# Revit family: Legrand_ElectricFireStopping_EZPathFirestopModule_Series33_Wall
name_source: partatom
category: Equipement spécialisé
units: mm (PartAtom-declared; Revit-internal decimal feet)

## family parameters
Cote de connecteur circulaire = Utiliser le diamètre
Couper avec des vides une fois chargée = Non
Hôte = Mur
Numéro OmniClass = 23.20.50.14
Partagée = Non
Point de calcul de pièce = Non
Titre OmniClass = Firestopping
Toujours verticalement = Oui
Type d'élément = Normal

## types (6) — shared parameters
AirLeakage(UL1479) = 0.14 m3/h 0% cable, 1.14 m3/h 100% cable
AssetType = Fixed
Classification(EN13501-2) = EI 120
ClassificationName = Uniclass2015
ClassificationValue = Ss_25_60_30
Code d'assemblage = D4030900
CodePerformance = Conforms to the European standard EN1366-3, BS476/20, ASTM E814 and DIN4102-9
Color = Red
Description = EZ-Path is a mechanical device that provides fully compliant fire stopping for power and data cable management pathways.
DocumentationInstallationGuide = https://www.legrand.co.uk
DocumentationLiterature = https://specifi.bimstore.co.uk
DocumentationMaintenance = https://www.legrand.co.uk
DocumentationTechnical = https://www.legrand.co.uk
DurationUnit = Years
EZ path 1 = Oui
EZ-PathDevice = Firestop-STI-EZ_Path-Series_33_Fire_Rated_Pathway
EZPathCutoutHeight = 50 mm
EZPathCutoutWidth = 68 mm
EZPathHeight = 75 mm
EZPathLeftCenterOfGanged = 264 mm
EZPathWidth = 75 mm
ExpansionBegins = 177 deg C
Fabricant = Legrand Electric Ltd
Features = The modules, which are suitable for all types of wall, can be assembled and installed horizontally or vertically to form a sturdy unit
Finish = Powder Coated
FireRating = Up to 4 Hr
FireResistance(EN1366-3) = 2 Hours
General Conditions of Use = https://export.legrand.com
IfcExportAs = IfcBuildingElementPart
IfcExportType = IfcBuildingElementPartTypeEnum.FIRESTOP
InServiceTemperature = Not to exceed 49 deg C
ManufacturerName = Legrand Electric Ltd
Material = 1.5mm thk Galv Steel
ModelNumber = CM250018
ModelNumberDevice = CM250018
ModelNumberExtensions = CM250078
ModelReference = EZ-Path® Permanent Automatic Mechanical Firestop System (Series 33) Wall
Modèle = EZ-Path® Permanent Automatic Mechanical Firestop System (Series 33) Wall
MountingPlateCutoutHeight = 75 mm
MountingPlateHeight = 102 mm
MountingPlateLeftCenterWidth = 51 mm
MountingPlateLeftCutoutCenterWidth = 38 mm
NBSDescription = Fire stopping systems
NBSObjectName = Legrand Electric Ltd - Fire stopping systems
NBSReference = 30-85-30
NoGanged = 7
NominalHeight = 78 mm
Note d'identification = P12
ProductPage = https://www.legrand.co.uk
ProductionYear = 2017
ReactionToFire(EN13501-1) = Class E
ReferencedStandard = CE Marking, EN 1366-3, ETA 130993
RetainingPlate = Firestop-STI-EZ_Path-Retaining_Plate
RetroPlate = Non
RetrofitHeightCenterline = 305 mm
RetrofitLowerHeight = 152 mm
RetrofitUpperHeight = 102 mm
RetrofitWidth = 203 mm
RoundPlateCutoutHeight = 75 mm
RoundPlateCutoutWidth = 76 mm
RoundPlateDia = 127 mm
SafetyDataSheet = https://files.stifirestop.com
SecondaryModelNumberExtensions = EZD33E
ShelfLife = No Limit
SoundInsulation(ASTME90) = STC 50
TestedSystems = https://www.legrand.co.uk
URL = https://www.legrand.co.uk
VolumeExpansion = 800%
WallCutoutHeight = 78 mm
WallLeftCutoutCenterWidth = 39 mm
WarrantyDescription = Firestop certification guaranteed throughout the entire lifetime of the electrical installation
WarrantyDurationLabor = 0
WarrantyDurationParts = 0
WarrantyDurationUnit = Years
Weight(Kg) = 1.16 kg
_BSBibleVersion = 15
_CurrentRevision = 2
_DistributedBy = www.bimstore.co.uk
zero-valued in all types: Elévation par défaut, ExpectedLife, MountingPlateWidthCenterline, RetrofitWidthCenterline, RoundPlateTopWidthCenterline, _BimSpecGuid

## per-type parameters (varying)
- 2 Devices with 2 Gang Plate Réf 2 x 250018 + 250120: BIMObjectName=Legrand_ElectricFireStopping_EZPathFirestopModule_Series33_Wall_2DeviceGangPlate; Commentaires du type=2 Devices with 2 Gang Plate; EZ path 2=Oui; EZ path 3=Non; EZ path 4=Non; EZ path 5=Non; EZ path 6=Non; EZ path 7=Non; ModelNumberBrackets=CM250120; MountingPlateCutoutWidth=152 mm; MountingPlateHeightCenterline=0 mm  [stored 0 ft]; MountingPlateWidth=178 mm; NoOfDevices=2; NoPlate=Non; NominalWidth=153 mm; PlateType=1; Region=Global; RoundPlate=Non; RoundPlateTopHeightCenterline=305 mm; SecondaryModelNumberBrackets=EZP233W; SecondaryModelNumberDevice=EZD33FWS; Shape=Rectangle (Series 33); Size=80x155mm; SquarePlate=Oui; TypeName=2 Devices with 2 Gang Plate; WallCutoutWidth=153 mm
- 3 Devices with 3 Gang Plate Réf 3 x 250018 + 250130: BIMObjectName=Legrand_ElectricFireStopping_EZPathFirestopModule_Series33_Wall_3DeviceGangPlate; Commentaires du type=3 Devices with 3 Gang Plate; EZ path 2=Oui; EZ path 3=Oui; EZ path 4=Non; EZ path 5=Non; EZ path 6=Non; EZ path 7=Non; ModelNumberBrackets=CM250130; MountingPlateCutoutWidth=227 mm; MountingPlateHeightCenterline=0 mm  [stored 0 ft]; MountingPlateWidth=253 mm; NoOfDevices=3; NoPlate=Non; NominalWidth=229 mm; PlateType=1; Region=Global; RoundPlate=Non; RoundPlateTopHeightCenterline=305 mm; SecondaryModelNumberBrackets=EZP333W; SecondaryModelNumberDevice=EZD33FWS; Shape=Rectangle (Series 33); Size=80x230mm; SquarePlate=Oui; TypeName=3 Devices with 3 Gang Plate; WallCutoutWidth=229 mm
- 4 Devices with 4 Gang Plate Réf 4 x 250018 + 250140: BIMObjectName=Legrand_ElectricFireStopping_EZPathFirestopModule_Series33_Wall_4DeviceGangPlate; Commentaires du type=4 Devices with 4 Gang Plate; EZ path 2=Oui; EZ path 3=Oui; EZ path 4=Oui; EZ path 5=Non; EZ path 6=Non; EZ path 7=Non; ModelNumberBrackets=CM250140; MountingPlateCutoutWidth=302 mm; MountingPlateHeightCenterline=0 mm  [stored 0 ft]; MountingPlateWidth=329 mm; NoOfDevices=4; NoPlate=Non; NominalWidth=304 mm; PlateType=1; Region=Global; RoundPlate=Non; RoundPlateTopHeightCenterline=305 mm; SecondaryModelNumberBrackets=EZP433W; SecondaryModelNumberDevice=EZD33FWS; Shape=Rectangle (Series 33); Size=80x305mm; SquarePlate=Oui; TypeName=4 Devices with 4 Gang Plate; WallCutoutWidth=304 mm
- 7 Devices with 7 Gang Plate Réf 7 x 250018 + 250170: BIMObjectName=Legrand_ElectricFireStopping_EZPathFirestopModule_Series33_Wall_7DeviceGangPlate; Commentaires du type=7 Devices with 7 Gang Plate; EZ path 2=Oui; EZ path 3=Oui; EZ path 4=Oui; EZ path 5=Oui; EZ path 6=Oui; EZ path 7=Oui; ModelNumberBrackets=CM250170; MountingPlateCutoutWidth=529 mm; MountingPlateHeightCenterline=0 mm  [stored 0 ft]; MountingPlateWidth=555 mm; NoOfDevices=7; NoPlate=Non; NominalWidth=530 mm; PlateType=1; Region=Global; RoundPlate=Non; RoundPlateTopHeightCenterline=305 mm; SecondaryModelNumberBrackets=EZP733W; SecondaryModelNumberDevice=EZD33FWS; Shape=Rectangle (Series 33); Size=80x540mm; SquarePlate=Oui; TypeName=7 Devices with 7 Gang Plate; WallCutoutWidth=530 mm
- 1 Device with Circular Plates Réf  250018 + 250240: BIMObjectName=Legrand_ElectricFireStopping_EZPathFirestopModule_Series33_Wall_1DeviceCircularPlate; Commentaires du type=1 Device with Circular Plates; EZ path 2=Non; EZ path 3=Non; EZ path 4=Non; EZ path 5=Non; EZ path 6=Non; EZ path 7=Non; ModelNumberBrackets=CM250240; MountingPlateCutoutWidth=76 mm; MountingPlateHeightCenterline=305 mm; MountingPlateWidth=102 mm; NoOfDevices=1; NoPlate=Non; NominalWidth=78 mm; PlateType=2; Region=Europe; RoundPlate=Oui; RoundPlateTopHeightCenterline=0 mm  [stored 0 ft]; SecondaryModelNumberBrackets=EZP133CWT; SecondaryModelNumberDevice=EZD33T; Shape=Square (Series 33); Size=80x80mm; SquarePlate=Non; TypeName=1 Device with Circular Plates; WallCutoutWidth=78 mm
- 1 Device Cast In Place (Concrete Walls Only - Grouted) Réf  250018: BIMObjectName=Legrand_ElectricFireStopping_EZPathFirestopModule_Series33_Wall_1DeviceCastInPlace; Commentaires du type=1 Device Cast In Place (Concrete Walls Only - Grouted); EZ path 2=Non; EZ path 3=Non; EZ path 4=Non; EZ path 5=Non; EZ path 6=Non; EZ path 7=Non; MountingPlateCutoutWidth=76 mm; MountingPlateHeightCenterline=0 mm  [stored 0 ft]; MountingPlateWidth=102 mm; NoOfDevices=1; NoPlate=Oui; NominalWidth=78 mm; PlateType=4; Region=Europe; RoundPlate=Non; RoundPlateTopHeightCenterline=305 mm; SecondaryModelNumberDevice=EZD33T; Shape=Square (Series 33); Size=80x80mm; SquarePlate=Non; TypeName=1 Device Cast In Place (Concrete Walls Only - Grouted); WallCutoutWidth=78 mm

note: [stored X ft] marks values corroborated as IEEE doubles in the binary element streams (Revit-internal decimal feet)

## geometry (parser evidence)
native form markers: Blend x2, Sweep x3
no freeform markers — native parametric forms only
